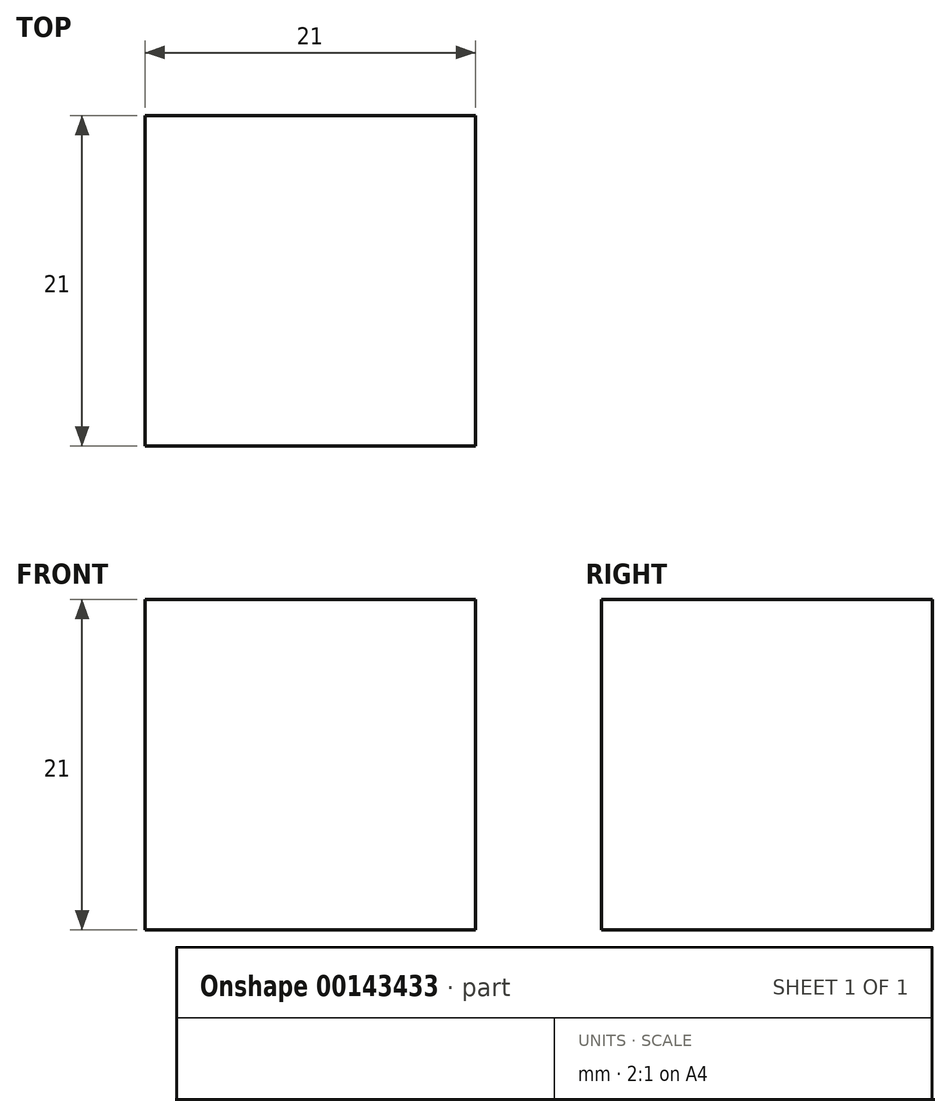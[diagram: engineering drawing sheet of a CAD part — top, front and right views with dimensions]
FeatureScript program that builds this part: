
annotation { "Feature Type Name" : "Feature", "Feature Type Description" : "" }
export const myFeature = defineFeature(function(context is Context, id is Id, definition is map)
    precondition{}
    {
        {
            var Q0;
            Q0=qCreatedBy(makeId("Front.planeOp"),FACE);
            var sketch = newSketch(context, id + "F0", { "sketchPlane" : qUnion([Q0])});
            skLineSegment(sketch, "E0.bottom", {"start": v(-10.5, -10.5) * mm, "end": v(10.5, -10.5) * mm});
            skLineSegment(sketch, "E0.top", {"start": v(-10.5, 10.5) * mm, "end": v(10.5, 10.5) * mm});
            skLineSegment(sketch, "E0.left", {"start": v(-10.5, -10.5) * mm, "end": v(-10.5, 10.5) * mm});
            skLineSegment(sketch, "E0.right", {"start": v(10.5, -10.5) * mm, "end": v(10.5, 10.5) * mm});
            skPoint(sketch, "E0.middle", {"position": v(0, 0) * mm});
            skSolve(sketch);
        }
        {
            var Q0;
            Q0 = qSketchRegion(id + "F0", true);
            extrude(context, id + "F1", {"entities" : qUnion([Q0]), "endBound" : BoundingType.SYMMETRIC, "depth" : 21 * mm});
        }
    });
